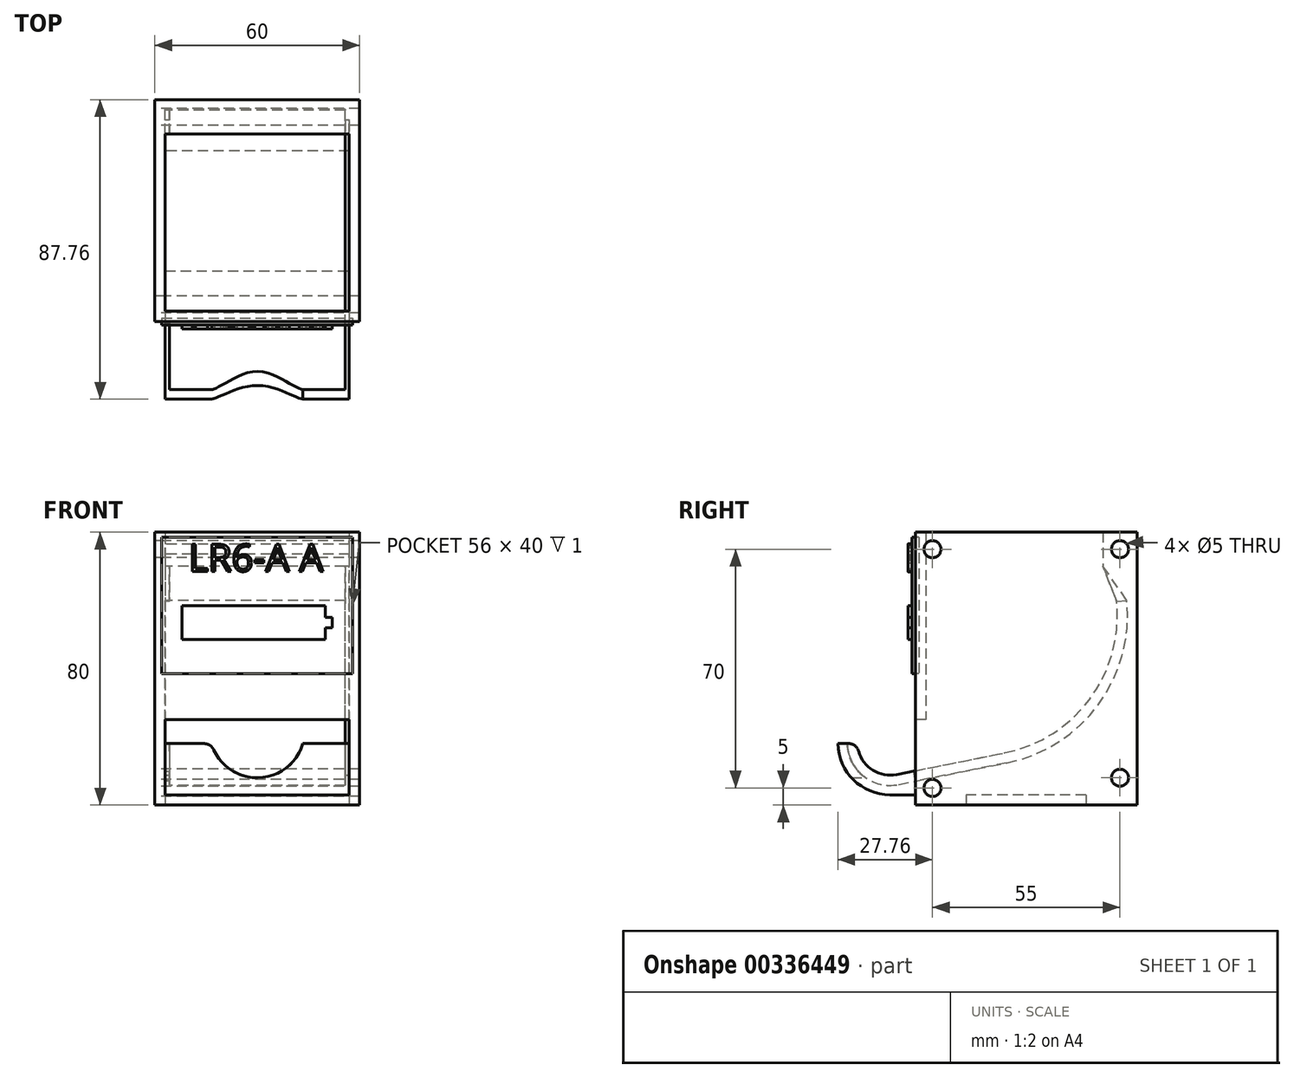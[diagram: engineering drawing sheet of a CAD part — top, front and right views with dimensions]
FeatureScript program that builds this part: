
annotation { "Feature Type Name" : "Feature", "Feature Type Description" : "" }
export const myFeature = defineFeature(function(context is Context, id is Id, definition is map)
    precondition{}
    {
        {
            var Q0;
            Q0=qCreatedBy(makeId("Top.planeOp"),FACE);
            var sketch = newSketch(context, id + "F0", { "sketchPlane" : qUnion([Q0])});
            skLineSegment(sketch, "E0", {"start": v(-30, 65) * mm, "end": v(-30, 0) * mm});
            skLineSegment(sketch, "E1", {"start": v(-30, 0) * mm, "end": v(30, 0) * mm});
            skLineSegment(sketch, "E2", {"start": v(30, 0) * mm, "end": v(30, 65) * mm});
            skLineSegment(sketch, "E3.0", {"start": v(-27, 65) * mm, "end": v(-27, 3) * mm});
            skLineSegment(sketch, "E4.0", {"start": v(-27, 3) * mm, "end": v(27, 3) * mm});
            skLineSegment(sketch, "E5.0", {"start": v(27, 3) * mm, "end": v(27, 65) * mm});
            skLineSegment(sketch, "E6", {"start": v(-30, 65) * mm, "end": v(-27, 65) * mm});
            skLineSegment(sketch, "E7", {"start": v(27, 65) * mm, "end": v(30, 65) * mm});
            skSolve(sketch);
        }
        {
            var Q0;
            Q0=qSketchRegion(id+"F0",true);
            extrude(context, id + "F1", {"entities" : qUnion([Q0]), "depth" : 80 * mm});
        }
        {
            var Q0;
            Q0=makeQuery(id+"F1.opExtrude","SWEPT_FACE",FACE,{"disambiguationData":[OSD([sQuery(id+"F0.wireOp",EDGE,"E1")])]});
            var sketch = newSketch(context, id + "F2", { "sketchPlane" : qUnion([Q0])});
            skLineSegment(sketch, "E8.bottom", {"start": v(-27, 3) * mm, "end": v(27, 3) * mm});
            skLineSegment(sketch, "E8.top", {"start": v(-27, 25) * mm, "end": v(27, 25) * mm});
            skLineSegment(sketch, "E8.left", {"start": v(-27, 3) * mm, "end": v(-27, 25) * mm});
            skLineSegment(sketch, "E8.right", {"start": v(27, 3) * mm, "end": v(27, 25) * mm});
            skSolve(sketch);
        }
        {
            var Q0;
            Q0=makeQuery(id+"F2.imprint","IMPRINT",FACE,{"disambiguationData":[TD([[makeQuery(id+"F2.imprint","IMPRINT",EDGE,{"derivedFrom":sQuery(id+"F2.wireOp",EDGE,"E8.bottom")}),1.0]])]});
            extrude(context, id + "F3", {"entities" : qUnion([Q0]), "operationType" : NewBodyOperationType.REMOVE, "endBound" : BoundingType.THROUGH_ALL, "oppositeDirection" : true, "depth" : 25 * mm});
        }
        {
            var Q0;
            {var subQ1=sQuery(id+"F0.wireOp",EDGE,"E4.0");Q0=makeQuery(id+"F3.boolean.opBoolean","SPLIT",FACE,{"disambiguationData":[TD([makeQuery(id+"F3.opExtrude","SWEPT_FACE",FACE,{"disambiguationData":[OSD([sQuery(id+"F2.wireOp",EDGE,"E8.bottom")])]})])],"derivedFrom":makeQuery(id+"F1.opExtrude","SWEPT_FACE",FACE,{"disambiguationData":[OSD([subQ1])]})});}
            extrude(context, id + "F4", {"entities" : qUnion([Q0]), "operationType" : NewBodyOperationType.ADD, "depth" : 11.8 * mm});
        }
        {
            var Q0;
            Q0=makeQuery(id+"F1.opExtrude","SWEPT_FACE",FACE,{"disambiguationData":[OSD([sQuery(id+"F0.wireOp",EDGE,"E1")])]});
            var sketch = newSketch(context, id + "F5", { "sketchPlane" : qUnion([Q0])});
            skLineSegment(sketch, "E9.bottom", {"start": v(-28, 78.5) * mm, "end": v(28, 78.5) * mm});
            skLineSegment(sketch, "E9.top", {"start": v(-28, 38.5) * mm, "end": v(28, 38.5) * mm});
            skLineSegment(sketch, "E9.left", {"start": v(-28, 78.5) * mm, "end": v(-28, 38.5) * mm});
            skLineSegment(sketch, "E9.right", {"start": v(28, 78.5) * mm, "end": v(28, 38.5) * mm});
            skSolve(sketch);
        }
        {
            var Q0;
            Q0 = qSketchRegion(id + "F5", true);
            extrude(context, id + "F6", {"entities" : qUnion([Q0]), "operationType" : NewBodyOperationType.REMOVE, "oppositeDirection" : true, "depth" : 1 * mm});
        }
        {
            var Q0;
            Q0 = qSketchRegion(id + "F5", true);
            extrude(context, id + "F7", {"entities" : qUnion([Q0]), "depth" : 1 * mm});
        }
        {
            var Q0;
            Q0=makeQuery(id+"F7.opExtrude","CAP_FACE",FACE,{"disambiguationData":[OSD([sQuery(id+"F5.wireOp",EDGE,"E9.bottom"),sQuery(id+"F5.wireOp",EDGE,"E9.top"),sQuery(id+"F5.wireOp",EDGE,"E9.left"),sQuery(id+"F5.wireOp",EDGE,"E9.right")])],"isStart":false});
            var sketch = newSketch(context, id + "F8", { "sketchPlane" : qUnion([Q0])});
            skText(sketch, "E10", { "text": "LR6-A A", "fontName": "OpenSans-Regular.ttf"});
            const initialGuessF8  = {"E10": [-0.02012, 0.0685, 1, 0, 0.008]};
            skSetInitialGuess(sketch, initialGuessF8);
            skSolve(sketch);
        }
        {
            var Q0;
            Q0=makeQuery(id+"F8.imprint","IMPRINT",FACE,{"disambiguationData":[TD([[makeQuery(id+"F8.imprint","IMPRINT",EDGE,{"derivedFrom":sQuery(id+"F8.wireOp",EDGE,"E10.sketch_text.stroke-0")}),1.0]])]});
            var sketch = newSketch(context, id + "F9", { "sketchPlane" : qUnion([Q0])});
            skLineSegment(sketch, "E11.bottom", {"start": v(-22, 58.5) * mm, "end": v(20, 58.5) * mm});
            skLineSegment(sketch, "E11.top", {"start": v(-22, 48.5) * mm, "end": v(20, 48.5) * mm});
            skLineSegment(sketch, "E11.left", {"start": v(-22, 58.5) * mm, "end": v(-22, 48.5) * mm});
            skLineSegment(sketch, "E11.right", {"start": v(20, 58.5) * mm, "end": v(20, 55) * mm});
            skPoint(sketch, "E12.oppositeSnap0", {"position": v(20, 53.5) * mm});
            skLineSegment(sketch, "E12.bottom", {"start": v(20, 55) * mm, "end": v(22, 55) * mm});
            skLineSegment(sketch, "E13.trimOffspring", {"start": v(20, 52) * mm, "end": v(20, 48.5) * mm});
            skLineSegment(sketch, "E14", {"start": v(22, 55) * mm, "end": v(22, 52) * mm});
            skLineSegment(sketch, "E15", {"start": v(22, 52) * mm, "end": v(20, 52) * mm});
            skSolve(sketch);
        }
        {
            var Q0;
            Q0=makeQuery(id+"F9.imprint","IMPRINT",FACE,{"disambiguationData":[TD([[makeQuery(id+"F9.imprint","IMPRINT",EDGE,{"derivedFrom":sQuery(id+"F9.wireOp",EDGE,"E11.bottom")}),-1.0]])]});
            extrude(context, id + "F10", {"entities" : qUnion([Q0]), "operationType" : NewBodyOperationType.ADD, "depth" : 1.2 * mm});
        }
        {
            var Q0;
            Q0=qSketchRegion(id+"F8",true);
            extrude(context, id + "F11", {"entities" : qUnion([Q0]), "operationType" : NewBodyOperationType.ADD, "depth" : 1.2 * mm});
        }
        {
            var Q0;
            Q0=makeQuery(id+"F1.opExtrude","SWEPT_FACE",FACE,{"disambiguationData":[OSD([sQuery(id+"F0.wireOp",EDGE,"E7")])]});
            var sketch = newSketch(context, id + "F12", { "sketchPlane" : qUnion([Q0])});
            skLineSegment(sketch, "E16.bottom", {"start": v(-27, 3) * mm, "end": v(27, 3) * mm});
            skLineSegment(sketch, "E16.top", {"start": v(-27, 0) * mm, "end": v(27, 0) * mm});
            skLineSegment(sketch, "E16.left", {"start": v(-27, 3) * mm, "end": v(-27, 0) * mm});
            skLineSegment(sketch, "E16.right", {"start": v(27, 3) * mm, "end": v(27, 0) * mm});
            skSolve(sketch);
        }
        {
            var Q0;
            Q0=makeQuery(id+"F12.imprint","IMPRINT",FACE,{"disambiguationData":[TD([[makeQuery(id+"F12.imprint","IMPRINT",EDGE,{"derivedFrom":sQuery(id+"F12.wireOp",EDGE,"E16.bottom")}),-1.0]])]});
            extrude(context, id + "F13", {"entities" : qUnion([Q0]), "operationType" : NewBodyOperationType.ADD, "oppositeDirection" : true, "depth" : 15 * mm});
        }
        {
            var Q0;
            Q0=qCreatedBy(makeId("Right.planeOp"),FACE);
            var sketch = newSketch(context, id + "F14", { "sketchPlane" : qUnion([Q0])});
            skLineSegment(sketch, "E17", {"start": v(65, 80) * mm, "end": v(55, 80) * mm});
            skLineSegment(sketch, "E18", {"start": v(55, 80) * mm, "end": v(55, 70) * mm});
            skLineSegment(sketch, "E19", {"start": v(55, 70) * mm, "end": v(62, 60) * mm});
            skLineSegment(sketch, "E20", {"start": v(65, 80) * mm, "end": v(65, 3) * mm});
            skLineSegment(sketch, "E21", {"start": v(65, 3) * mm, "end": v(-7.46, 3) * mm});
            skArc(sketch, "E22", {"start": v(26.86, 12.37) * mm, "mid": v(53.63, 29.4) * mm, "end": v(62, 60) * mm});
            skLineSegment(sketch, "E23", {"start": v(-22.76, 18) * mm, "end": v(-20, 18) * mm});
            skLineSegment(sketch, "E24", {"start": v(26.86, 12.37) * mm, "end": v(-5, 6) * mm});
            skArc(sketch, "E25", {"start": v(-5, 6) * mm, "mid": v(-15.3, 8.5) * mm, "end": v(-20, 18) * mm});
            skArc(sketch, "E26", {"start": v(-7.46, 3) * mm, "mid": v(-18.17, 7.38) * mm, "end": v(-22.76, 18) * mm});
            skPoint(sketch, "E27", {"position": v(0, 7) * mm});
            skSolve(sketch);
        }
        {
            var Q0;
            Q0=makeQuery(id+"F14.imprint","IMPRINT",FACE,{"disambiguationData":[TD([[makeQuery(id+"F14.imprint","IMPRINT",EDGE,{"derivedFrom":sQuery(id+"F14.wireOp",EDGE,"E17")}),1.0]])]});
            extrude(context, id + "F15", {"entities" : qUnion([Q0]), "endBound" : BoundingType.SYMMETRIC, "depth" : 54 * mm});
        }
        {
            var Q0;
            Q0=qCreatedBy(makeId("Right.planeOp"),FACE);
            var sketch = newSketch(context, id + "F16", { "sketchPlane" : qUnion([Q0])});
            skCircle(sketch, "E28", {"center": v(60, 75) * mm, "radius": 2.5 * mm});
            skCircle(sketch, "E29", {"center": v(60, 8) * mm, "radius": 2.5 * mm});
            skCircle(sketch, "E30", {"center": v(5, 75) * mm, "radius": 2.5 * mm});
            skCircle(sketch, "E31", {"center": v(5, 5) * mm, "radius": 2.5 * mm});
            skSolve(sketch);
        }
        {
            var Q0;
            Q0 = qSketchRegion(id + "F16", true);
            extrude(context, id + "F17", {"entities" : qUnion([Q0]), "operationType" : NewBodyOperationType.REMOVE, "endBound" : BoundingType.SYMMETRIC, "depth" : 60 * mm});
        }
        {
            var Q0;
            Q0=makeQuery(id+"F15.opExtrude","SWEPT_FACE",FACE,{"disambiguationData":[OSD([sQuery(id+"F14.wireOp",EDGE,"E23")])]});
            var sketch = newSketch(context, id + "F18", { "sketchPlane" : qUnion([Q0])});
            skLineSegment(sketch, "E32.bottom", {"start": v(25.8, -20) * mm, "end": v(27, -20) * mm});
            skLineSegment(sketch, "E32.top", {"start": v(25.8, -17) * mm, "end": v(27, -17) * mm});
            skLineSegment(sketch, "E32.left", {"start": v(25.8, -20) * mm, "end": v(25.8, -17) * mm});
            skLineSegment(sketch, "E32.right", {"start": v(27, -20) * mm, "end": v(27, -17) * mm});
            skLineSegment(sketch, "E33.bottom", {"start": v(-27, -20) * mm, "end": v(-25.8, -20) * mm});
            skLineSegment(sketch, "E33.top", {"start": v(-27, -17) * mm, "end": v(-25.8, -17) * mm});
            skLineSegment(sketch, "E33.left", {"start": v(-27, -20) * mm, "end": v(-27, -17) * mm});
            skLineSegment(sketch, "E33.right", {"start": v(-25.8, -20) * mm, "end": v(-25.8, -17) * mm});
            skSolve(sketch);
        }
        {
            var Q0;
            Q0=makeQuery(id+"F18.imprint","IMPRINT",FACE,{"disambiguationData":[TD([[makeQuery(id+"F18.imprint","IMPRINT",EDGE,{"derivedFrom":sQuery(id+"F18.wireOp",EDGE,"E32.bottom")}),-1.0]])]});
            var Q1;
            Q1=makeQuery(id+"F15.opExtrude","CAP_EDGE",EDGE,{"disambiguationData":[OSD([sQuery(id+"F14.wireOp",EDGE,"E25")])],"isStart":false});
            var Q2;
            Q2=makeQuery(id+"F15.opExtrude","CAP_EDGE",EDGE,{"disambiguationData":[OSD([sQuery(id+"F14.wireOp",EDGE,"E24")])],"isStart":false});
            var Q3;
            Q3=makeQuery(id+"F15.opExtrude","CAP_EDGE",EDGE,{"disambiguationData":[OSD([sQuery(id+"F14.wireOp",EDGE,"E22")])],"isStart":false});
            sweep(context, id + "F19", {"operationType" : NewBodyOperationType.ADD, "profiles" : qUnion([Q0]), "path" : qUnion([Q1, Q2, Q3])});
        }
        {
            var Q0;
            Q0=makeQuery(id+"F18.imprint","IMPRINT",FACE,{"disambiguationData":[TD([[makeQuery(id+"F18.imprint","IMPRINT",EDGE,{"derivedFrom":sQuery(id+"F18.wireOp",EDGE,"E33.bottom")}),-1.0]])]});
            var Q1;
            Q1=makeQuery(id+"F15.opExtrude","CAP_EDGE",EDGE,{"disambiguationData":[OSD([sQuery(id+"F14.wireOp",EDGE,"E25")])],"isStart":true});
            var Q2;
            Q2=makeQuery(id+"F15.opExtrude","CAP_EDGE",EDGE,{"disambiguationData":[OSD([sQuery(id+"F14.wireOp",EDGE,"E24")])],"isStart":true});
            var Q3;
            Q3=makeQuery(id+"F15.opExtrude","CAP_EDGE",EDGE,{"disambiguationData":[OSD([sQuery(id+"F14.wireOp",EDGE,"E22")])],"isStart":true});
            sweep(context, id + "F20", {"operationType" : NewBodyOperationType.ADD, "profiles" : qUnion([Q0]), "path" : qUnion([Q1, Q2, Q3])});
        }
        {
            var Q0;
            Q0=qCreatedBy(makeId("Front.planeOp"),FACE);
            var sketch = newSketch(context, id + "F21", { "sketchPlane" : qUnion([Q0])});
            skArc(sketch, "E34", {"start": v(-13.42, 18) * mm, "mid": v(0, 8) * mm, "end": v(13.42, 18) * mm});
            skLineSegment(sketch, "E35", {"start": v(-13.42, 18) * mm, "end": v(13.42, 18) * mm});
            skSolve(sketch);
        }
        {
            var Q0;
            Q0=makeQuery(id+"F21.imprint","IMPRINT",FACE,{"disambiguationData":[TD([[makeQuery(id+"F21.imprint","IMPRINT",EDGE,{"derivedFrom":sQuery(id+"F21.wireOp",EDGE,"E34")}),1.0]])]});
            extrude(context, id + "F22", {"entities" : qUnion([Q0]), "operationType" : NewBodyOperationType.REMOVE, "endBound" : BoundingType.THROUGH_ALL, "depth" : 25 * mm});
        }
        {
            var Q0;
            {var subQ0=sQuery(id+"F21.wireOp",EDGE,"E35");var subQ1=sQuery(id+"F21.wireOp",EDGE,"E34");Q0=makeQuery(id+"F22.boolean.opBoolean","COPY",EDGE,{"derivedFrom":makeQuery(id+"F22.opExtrude","SWEPT_EDGE",EDGE,{"disambiguationData":[OSD([subQ1,subQ0]),TDD([makeQuery(id+"F21.imprint","INTERSECT",VERTEX,{"disambiguationData":[OD(1.0)],"derivedFrom":[subQ1,subQ0]})])]})});}
            var Q1;
            {var subQ0=sQuery(id+"F21.wireOp",EDGE,"E35");var subQ1=sQuery(id+"F21.wireOp",EDGE,"E34");Q1=makeQuery(id+"F22.boolean.opBoolean","COPY",EDGE,{"derivedFrom":makeQuery(id+"F22.opExtrude","SWEPT_EDGE",EDGE,{"disambiguationData":[OSD([subQ1,subQ0]),TDD([makeQuery(id+"F21.imprint","INTERSECT",VERTEX,{"disambiguationData":[OD(0.0)],"derivedFrom":[subQ1,subQ0]})])]})});}
            fillet(context, id + "F23", {"entities" : qUnion([Q0, Q1]), "radius" : 3.1 * mm, "tangentPropagation" : true, "allowEdgeOverflow" : false});
        }
        {
            var Q0;
            Q0=makeQuery(id+"F20.opSweep","CAP_EDGE",EDGE,{"disambiguationData":[OSD([sQuery(id+"F14.wireOp",EDGE,"E23"),sQuery(id+"F14.wireOp",EDGE,"E25"),sQuery(id+"F18.wireOp",EDGE,"E33.top")])],"isStart":true});
            var Q1;
            Q1=makeQuery(id+"F19.opSweep","CAP_EDGE",EDGE,{"disambiguationData":[OSD([sQuery(id+"F14.wireOp",EDGE,"E23"),sQuery(id+"F14.wireOp",EDGE,"E25"),sQuery(id+"F18.wireOp",EDGE,"E32.top")])],"isStart":true});
            fillet(context, id + "F24", {"entities" : qUnion([Q0, Q1]), "radius" : 3 * mm, "tangentPropagation" : true, "allowEdgeOverflow" : false});
        }
        {
            var Q0;
            {var subQ0=sQuery(id+"F14.wireOp",EDGE,"E25");Q0=makeQuery(id+"F19.boolean.opBoolean","MERGE",FACE,{"derivedFrom":[makeQuery(id+"F15.opExtrude","CAP_FACE",FACE,{"disambiguationData":[OSD([sQuery(id+"F14.wireOp",EDGE,"E17"),sQuery(id+"F14.wireOp",EDGE,"E18"),sQuery(id+"F14.wireOp",EDGE,"E19"),sQuery(id+"F14.wireOp",EDGE,"E20"),sQuery(id+"F14.wireOp",EDGE,"E21"),sQuery(id+"F14.wireOp",EDGE,"E22"),sQuery(id+"F14.wireOp",EDGE,"E23"),sQuery(id+"F14.wireOp",EDGE,"E24"),subQ0,sQuery(id+"F14.wireOp",EDGE,"E26")])],"isStart":false}),makeQuery(id+"F19.opSweep","SWEPT_FACE",FACE,{"disambiguationData":[OSD([subQ0,sQuery(id+"F18.wireOp",EDGE,"E32.right")])]})]});}
            var sketch = newSketch(context, id + "F25", { "sketchPlane" : qUnion([Q0])});
            skLineSegment(sketch, "E36", {"start": v(59, 59.77) * mm, "end": v(55, 70) * mm});
            skLineSegment(sketch, "E37", {"start": v(55, 70) * mm, "end": v(62, 60) * mm});
            skLineSegment(sketch, "E38", {"start": v(62, 60) * mm, "end": v(59, 59.77) * mm});
            skSolve(sketch);
        }
        {
            var Q0;
            Q0=makeQuery(id+"F25.imprint","IMPRINT",FACE,{"disambiguationData":[TD([[makeQuery(id+"F25.imprint","IMPRINT",EDGE,{"derivedFrom":sQuery(id+"F25.wireOp",EDGE,"E36")}),-1.0]])]});
            extrude(context, id + "F26", {"entities" : qUnion([Q0]), "operationType" : NewBodyOperationType.ADD, "oppositeDirection" : true, "depth" : 1.2 * mm});
        }
        {
            var Q0;
            {var subQ0=sQuery(id+"F14.wireOp",EDGE,"E25");Q0=makeQuery(id+"F20.boolean.opBoolean","MERGE",FACE,{"derivedFrom":[makeQuery(id+"F15.opExtrude","CAP_FACE",FACE,{"disambiguationData":[OSD([sQuery(id+"F14.wireOp",EDGE,"E17"),sQuery(id+"F14.wireOp",EDGE,"E18"),sQuery(id+"F14.wireOp",EDGE,"E19"),sQuery(id+"F14.wireOp",EDGE,"E20"),sQuery(id+"F14.wireOp",EDGE,"E21"),sQuery(id+"F14.wireOp",EDGE,"E22"),sQuery(id+"F14.wireOp",EDGE,"E23"),sQuery(id+"F14.wireOp",EDGE,"E24"),subQ0,sQuery(id+"F14.wireOp",EDGE,"E26")])],"isStart":true}),makeQuery(id+"F20.opSweep","SWEPT_FACE",FACE,{"disambiguationData":[OSD([subQ0,sQuery(id+"F18.wireOp",EDGE,"E33.left")])]})]});}
            var sketch = newSketch(context, id + "F27", { "sketchPlane" : qUnion([Q0])});
            skLineSegment(sketch, "E39", {"start": v(-55, 70) * mm, "end": v(-59, 59.77) * mm});
            skLineSegment(sketch, "E40", {"start": v(-59, 59.77) * mm, "end": v(-62, 60) * mm});
            skLineSegment(sketch, "E41", {"start": v(-62, 60) * mm, "end": v(-55, 70) * mm});
            skSolve(sketch);
        }
        {
            var Q0;
            Q0=makeQuery(id+"F27.imprint","IMPRINT",FACE,{"disambiguationData":[TD([[makeQuery(id+"F27.imprint","IMPRINT",EDGE,{"derivedFrom":sQuery(id+"F27.wireOp",EDGE,"E39")}),-1.0]])]});
            extrude(context, id + "F28", {"entities" : qUnion([Q0]), "operationType" : NewBodyOperationType.ADD, "oppositeDirection" : true, "depth" : 1.2 * mm});
        }
        {
            var Q0;
            {var subQ0=sQuery(id+"F18.wireOp",EDGE,"E32.top");var subQ1=sQuery(id+"F14.wireOp",EDGE,"E22");Q0=makeQuery(id+"F26.boolean.opBoolean","MERGE",EDGE,{"derivedFrom":[makeQuery(id+"F19.opSweep","CAP_EDGE",EDGE,{"disambiguationData":[OSD([sQuery(id+"F14.wireOp",EDGE,"E19"),subQ1,subQ0])],"isStart":false}),makeQuery(id+"F26.opExtrude","SWEPT_EDGE",EDGE,{"disambiguationData":[OSD([subQ1,subQ0,sQuery(id+"F18.wireOp",EDGE,"E32.right"),sQuery(id+"F25.wireOp",EDGE,"E36"),sQuery(id+"F25.wireOp",EDGE,"E38")])]})]});}
            var Q1;
            {var subQ0=sQuery(id+"F18.wireOp",EDGE,"E33.top");var subQ1=sQuery(id+"F14.wireOp",EDGE,"E22");Q1=makeQuery(id+"F28.boolean.opBoolean","MERGE",EDGE,{"derivedFrom":[makeQuery(id+"F20.opSweep","CAP_EDGE",EDGE,{"disambiguationData":[OSD([sQuery(id+"F14.wireOp",EDGE,"E19"),subQ1,subQ0])],"isStart":false}),makeQuery(id+"F28.opExtrude","SWEPT_EDGE",EDGE,{"disambiguationData":[OSD([subQ1,subQ0,sQuery(id+"F18.wireOp",EDGE,"E33.left"),sQuery(id+"F27.wireOp",EDGE,"E39"),sQuery(id+"F27.wireOp",EDGE,"E40")])]})]});}
            fillet(context, id + "F29", {"entities" : qUnion([Q0, Q1]), "radius" : 5 * mm, "tangentPropagation" : true, "allowEdgeOverflow" : false});
        }
    });
